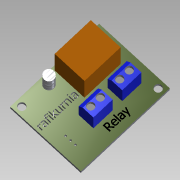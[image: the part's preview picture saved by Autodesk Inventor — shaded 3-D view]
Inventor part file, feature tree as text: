
AUTODESK INVENTOR PART (.ipt)
format: ipt  version: 2015 SP1 (Build 190203100, 203)  size: 388,096 bytes
history: native  units: mm
features: extrude x6, sketch x3, chamfer x1
ambient origin geometry x8: Origin, YZ Plane, XZ Plane, XY Plane, X Axis, Y Axis, Z Axis, Center Point
bodies: Solid1 (feature_tree)
feature tree (10):
  sketch  "Sketch1"  dims[d0=46.25mm d1=36.41mm]
  extrude  "Extrusion1"  Depth=36.41mm
  extrude  "Extrusion2"  Depth=3.0mm
  extrude  "Extrusion3"  Depth=3.0mm
  extrude  "Extrusion4"  Depth=3.0mm
  chamfer  "Chamfer1"  Distance=18.79mm
  extrude  "Extrusion5"  Depth=15.32mm
  sketch  "Sketch2"  dims[d5=3.0mm d6=3.0mm]
  extrude  "Extrusion6"  Depth=24.243896mm
  sketch  "Sketch3"  dims[d7=3.5mm d8=3.0mm d9=3.0mm d10=18.79mm d11=15.32mm d12=24.243896mm d13=24.243896mm d14=5.81mm d15=1.5mm d16=1.0mm d17=8.76mm d18=6.0mm d19=1.0mm d20=1.0mm d21=2.54mm d22=2.54mm d23=5.0mm d25=3.5mm d26=3.5mm d28=5.0mm d29=10.0mm d30=7.5mm d31=3.5mm d32=3.5mm d33=5.0mm d34=2.5mm d35=10.0mm d36=7.5mm d37=1.6mm d38=0.0mm d39=17.44mm d40=0.0mm d41=10.15mm d42=0.0mm d43=11.88mm d44=0.0mm d45=2.0mm d46=2.0mm d47=45.0deg d48=10.0mm d49=0.0mm d50=10.0mm d51=0.0mm]
